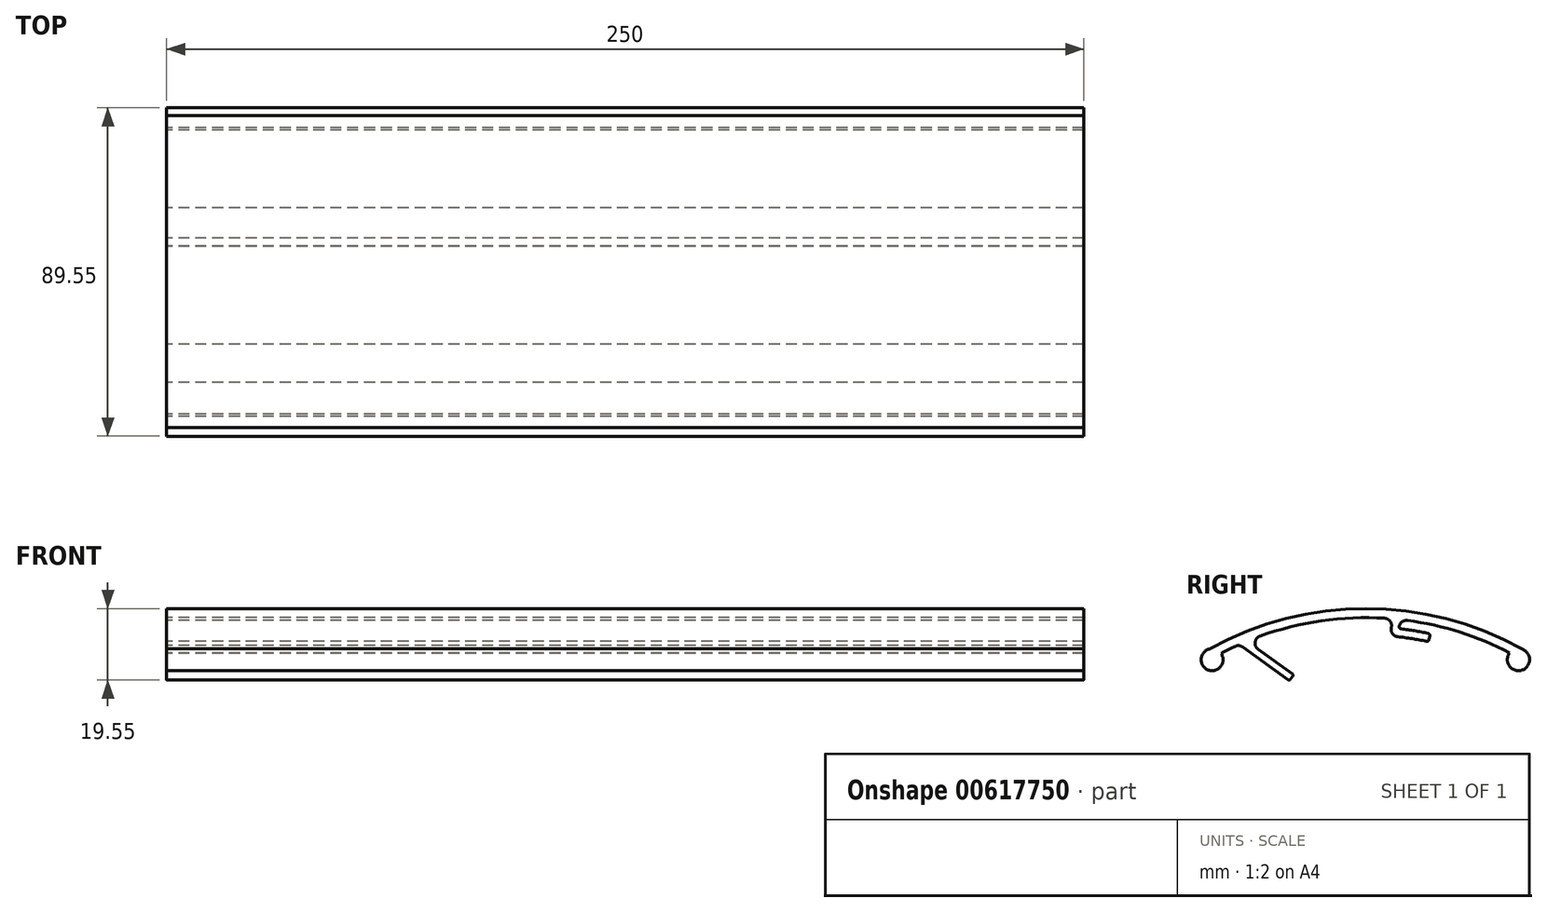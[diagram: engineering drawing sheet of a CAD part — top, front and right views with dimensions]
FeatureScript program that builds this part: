
annotation { "Feature Type Name" : "Feature", "Feature Type Description" : "" }
export const myFeature = defineFeature(function(context is Context, id is Id, definition is map)
    precondition{}
    {
        {
            var Q0;
            Q0=qCreatedBy(makeId("Right.planeOp"),FACE);
            var sketch = newSketch(context, id + "F0", { "sketchPlane" : qUnion([Q0])});
            skArc(sketch, "E0", {"start": v(41.73, -2.52) * mm, "mid": v(45.08, -7.25) * mm, "end": v(45.04, -1.45) * mm});
            skArc(sketch, "E1", {"start": v(-39.98, -1.45) * mm, "mid": v(-40.45, -7.19) * mm, "end": v(-36.93, -2.64) * mm});
            skArc(sketch, "E2", {"start": v(45.04, -1.45) * mm, "mid": v(2.53, 9.58) * mm, "end": v(-39.98, -1.45) * mm});
            skArc(sketch, "E3.0", {"start": v(41.73, -2.52) * mm, "mid": v(28.18, 3.11) * mm, "end": v(13.86, 6.32) * mm});
            skArc(sketch, "E4", {"start": v(-18.1, -9.83) * mm, "mid": v(-17.7, -9.33) * mm, "end": v(-17.34, -8.82) * mm});
            skPoint(sketch, "E5.endSnap0", {"position": v(45.08, -7.25) * mm});
            skLineSegment(sketch, "E6.MirrorCS", {"start": v(-26.84, -1.48) * mm, "end": v(-17.43, -8.3) * mm});
            skLineSegment(sketch, "E7.trimOffspring", {"start": v(-31.02, -0.92) * mm, "end": v(-18.62, -9.9) * mm});
            skPoint(sketch, "E8.start.orphan", {"position": v(-36.93, 3.35) * mm});
            skArc(sketch, "E9.trimOffspring", {"start": v(-33.03, -0.72) * mm, "mid": v(-35, -1.66) * mm, "end": v(-36.93, -2.64) * mm});
            skPoint(sketch, "E10.visualSharp", {"position": v(-29.82, 0.68) * mm});
            skArc(sketch, "E10.filletArc", {"start": v(-26.34, 2.02) * mm, "mid": v(-27.64, 0.42) * mm, "end": v(-26.84, -1.48) * mm});
            skPoint(sketch, "E11.visualSharp", {"position": v(-31.96, -0.24) * mm});
            skArc(sketch, "E11.filletArc", {"start": v(-31.02, -0.92) * mm, "mid": v(-32, -0.55) * mm, "end": v(-33.03, -0.72) * mm});
            skPoint(sketch, "E12.visualSharp", {"position": v(-18.33, -10.11) * mm});
            skArc(sketch, "E12.filletArc", {"start": v(-18.62, -9.9) * mm, "mid": v(-18.34, -9.97) * mm, "end": v(-18.1, -9.83) * mm});
            skPoint(sketch, "E13.visualSharp", {"position": v(-17.13, -8.51) * mm});
            skArc(sketch, "E13.filletArc", {"start": v(-17.34, -8.82) * mm, "mid": v(-17.27, -8.54) * mm, "end": v(-17.43, -8.3) * mm});
            skArc(sketch, "E14.0", {"start": v(19.5, 2.81) * mm, "mid": v(15.84, 3.5) * mm, "end": v(12.14, 4.02) * mm});
            skArc(sketch, "E15.0", {"start": v(19.05, 0.64) * mm, "mid": v(15.15, 1.36) * mm, "end": v(11.22, 1.89) * mm});
            skLineSegment(sketch, "E16", {"start": v(9.53, 4.58) * mm, "end": v(9.47, 4.22) * mm});
            skLineSegment(sketch, "E17", {"start": v(11.62, 4.68) * mm, "end": v(11.52, 4.09) * mm});
            skArc(sketch, "E18.trimOffspring", {"start": v(7.68, 6.92) * mm, "mid": v(-9.58, 6.21) * mm, "end": v(-26.34, 2.02) * mm});
            skPoint(sketch, "E19.visualSharp", {"position": v(9.9, 6.76) * mm});
            skArc(sketch, "E19.filletArc", {"start": v(9.84, 6.35) * mm, "mid": v(9.76, 6.65) * mm, "end": v(9.5, 6.8) * mm});
            skArc(sketch, "E20.filletArc", {"start": v(9.53, 4.58) * mm, "mid": v(9.13, 6.17) * mm, "end": v(7.68, 6.92) * mm});
            skPoint(sketch, "E21.visualSharp", {"position": v(9.1, 2.09) * mm});
            skArc(sketch, "E21.filletArc", {"start": v(9.47, 4.22) * mm, "mid": v(9.84, 2.67) * mm, "end": v(11.22, 1.89) * mm});
            skPoint(sketch, "E22.visualSharp", {"position": v(11.95, 6.56) * mm});
            skArc(sketch, "E22.filletArc", {"start": v(13.86, 6.32) * mm, "mid": v(12.43, 5.96) * mm, "end": v(11.63, 4.72) * mm});
            skArc(sketch, "E23.filletArc", {"start": v(11.63, 4.72) * mm, "mid": v(11.73, 4.26) * mm, "end": v(12.14, 4.02) * mm});
            skLineSegment(sketch, "E24", {"start": v(19.75, 1.1) * mm, "end": v(19.96, 2.11) * mm});
            skArc(sketch, "E25.filletArc", {"start": v(19.96, 2.11) * mm, "mid": v(19.88, 2.56) * mm, "end": v(19.5, 2.81) * mm});
            skPoint(sketch, "E26.visualSharp", {"position": v(19.63, 0.51) * mm});
            skArc(sketch, "E26.filletArc", {"start": v(19.05, 0.64) * mm, "mid": v(19.5, 0.72) * mm, "end": v(19.75, 1.1) * mm});
            skSolve(sketch);
        }
        {
            var Q0;
            Q0 = qSketchRegion(id + "F0", true);
            extrude(context, id + "F1", {"entities" : qUnion([Q0]), "depth" : 250 * mm, "offsetDistance" : 25 * mm});
        }
    });
